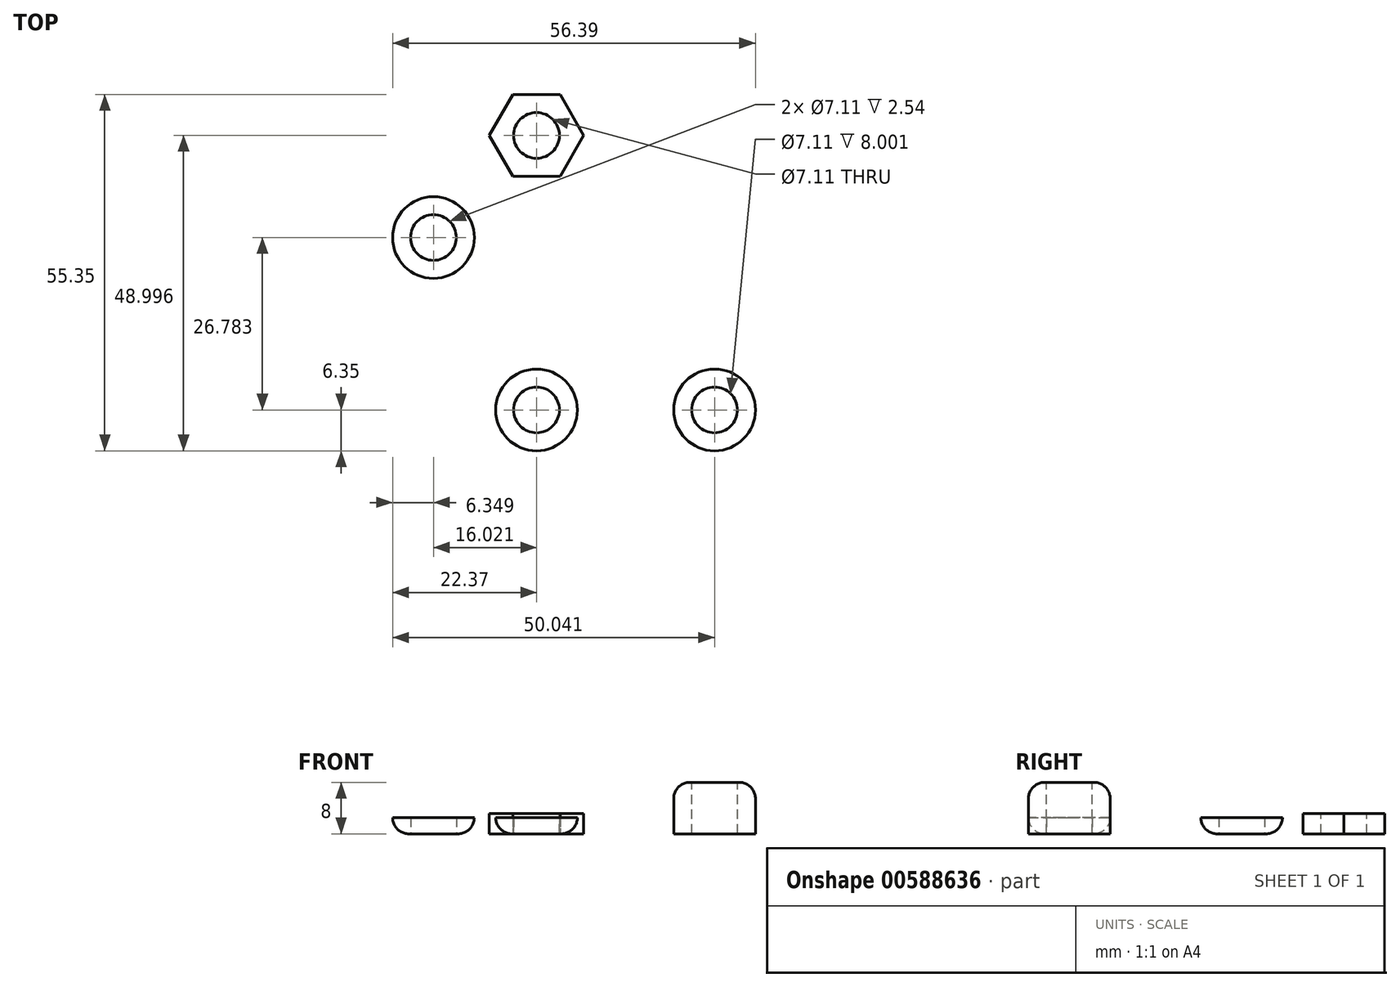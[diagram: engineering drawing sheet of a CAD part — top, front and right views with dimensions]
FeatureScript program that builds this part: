
annotation { "Feature Type Name" : "Feature", "Feature Type Description" : "" }
export const myFeature = defineFeature(function(context is Context, id is Id, definition is map)
    precondition{}
    {
        {
            var Q0;
            Q0=qCreatedBy(makeId("Top.planeOp"),FACE);
            var sketch = newSketch(context, id + "F0", { "sketchPlane" : qUnion([Q0])});
            skCircle(sketch, "E0", {"center": v(0, 0) * mm, "radius": 6.35 * mm});
            skCircle(sketch, "E1", {"center": v(-16.02, 26.78) * mm, "radius": 6.35 * mm});
            skSolve(sketch);
        }
        {
            var Q0;
            Q0 = qSketchRegion(id + "F0", true);
            extrude(context, id + "F1", {"entities" : qUnion([Q0]), "depth" : 2.54 * mm, "offsetDistance" : 25.4 * mm});
        }
        {
            var Q0;
            Q0=makeQuery(id+"F1.opExtrude","CAP_EDGE",EDGE,{"disambiguationData":[OSD([sQuery(id+"F0.wireOp",EDGE,"E0")])],"isStart":true});
            var Q1;
            Q1=makeQuery(id+"F1.opExtrude","CAP_EDGE",EDGE,{"disambiguationData":[OSD([sQuery(id+"F0.wireOp",EDGE,"E1")])],"isStart":true});
            fillet(context, id + "F2", {"entities" : qUnion([Q0, Q1]), "radius" : 2.54 * mm, "tangentPropagation" : true, "allowEdgeOverflow" : false});
        }
        {
            var Q0;
            Q0=makeQuery(id+"F1.opExtrude","CAP_FACE",FACE,{"disambiguationData":[OSD([sQuery(id+"F0.wireOp",EDGE,"E0")])],"isStart":true});
            var sketch = newSketch(context, id + "F3", { "sketchPlane" : qUnion([Q0])});
            skCircle(sketch, "E2", {"center": v(0, 0) * mm, "radius": 3.56 * mm});
            skSolve(sketch);
        }
        {
            var Q0;
            Q0 = qSketchRegion(id + "F3", true);
            extrude(context, id + "F4", {"entities" : qUnion([Q0]), "operationType" : NewBodyOperationType.REMOVE, "oppositeDirection" : true, "depth" : 2.54 * mm, "offsetDistance" : 25.4 * mm});
        }
        {
            var Q0;
            Q0=makeQuery(id+"F1.opExtrude","CAP_FACE",FACE,{"disambiguationData":[OSD([sQuery(id+"F0.wireOp",EDGE,"E1")])],"isStart":true});
            var sketch = newSketch(context, id + "F5", { "sketchPlane" : qUnion([Q0])});
            skCircle(sketch, "E3", {"center": v(-16.02, -26.78) * mm, "radius": 3.56 * mm});
            skSolve(sketch);
        }
        {
            var Q0;
            Q0 = qSketchRegion(id + "F5", true);
            extrude(context, id + "F6", {"entities" : qUnion([Q0]), "operationType" : NewBodyOperationType.REMOVE, "oppositeDirection" : true, "depth" : 2.54 * mm, "offsetDistance" : 25.4 * mm});
        }
        {
            var Q0;
            Q0=qCreatedBy(makeId("Top.planeOp"),FACE);
            var sketch = newSketch(context, id + "F7", { "sketchPlane" : qUnion([Q0])});
            skCircle(sketch, "E4", {"center": v(27.67, 0) * mm, "radius": 6.35 * mm});
            skSolve(sketch);
        }
        {
            var Q0;
            Q0=makeQuery(id+"F7.imprint","IMPRINT",FACE,{"disambiguationData":[TD([[makeQuery(id+"F7.imprint","IMPRINT",EDGE,{"derivedFrom":sQuery(id+"F7.wireOp",EDGE,"E4")}),1.0]])]});
            extrude(context, id + "F8", {"entities" : qUnion([Q0]), "depth" : 8 * mm, "offsetDistance" : 25.4 * mm});
        }
        {
            var Q0;
            Q0=makeQuery(id+"F8.opExtrude","CAP_EDGE",EDGE,{"disambiguationData":[OSD([sQuery(id+"F7.wireOp",EDGE,"TgdO63bO-GpAG-Yatk-n7lf-2ucI2Jy1ILUc")])],"isStart":false});
            var Q1;
            Q1=makeQuery(id+"F8.opExtrude","CAP_EDGE",EDGE,{"disambiguationData":[OSD([sQuery(id+"F7.wireOp",EDGE,"E4")])],"isStart":false});
            fillet(context, id + "F9", {"entities" : qUnion([Q0, Q1]), "radius" : 2.54 * mm, "tangentPropagation" : true, "allowEdgeOverflow" : false});
        }
        {
            var Q0;
            Q0=makeQuery(id+"F8.opExtrude","CAP_FACE",FACE,{"disambiguationData":[OSD([sQuery(id+"F7.wireOp",EDGE,"E4")])],"isStart":false});
            var sketch = newSketch(context, id + "F10", { "sketchPlane" : qUnion([Q0])});
            skSolve(sketch);
        }
        {
            var Q0;
            {var subQ0=sQuery(id+"F7.wireOp",EDGE,"E4");Q0=makeQuery(id+"F10.imprint","IMPRINT",FACE,{"disambiguationData":[TD([[makeQuery(id+"F10.imprint","IMPRINT",EDGE,{"derivedFrom":makeQuery(id+"F9.opFillet","BLEND_EDGE",EDGE,{"blendedFrom":[makeQuery(id+"F8.opExtrude","CAP_EDGE",EDGE,{"disambiguationData":[OSD([subQ0])],"isStart":false}),makeQuery(id+"F8.opExtrude","CAP_FACE",FACE,{"disambiguationData":[OSD([subQ0])],"isStart":false})],"blendedInto":[makeQuery(id+"F8.opExtrude","CAP_FACE",FACE,{"disambiguationData":[OSD([subQ0])],"isStart":false})]})}),1.0]])]});}
            var sketch = newSketch(context, id + "F11", { "sketchPlane" : qUnion([Q0])});
            skCircle(sketch, "E5", {"center": v(27.67, 0) * mm, "radius": 3.56 * mm});
            skSolve(sketch);
        }
        {
            var Q0;
            Q0 = qSketchRegion(id + "F11", true);
            extrude(context, id + "F12", {"entities" : qUnion([Q0]), "operationType" : NewBodyOperationType.REMOVE, "oppositeDirection" : true, "depth" : 11.15 * mm, "offsetDistance" : 25.4 * mm});
        }
        {
            var Q0;
            Q0=qCreatedBy(makeId("Top.planeOp"),FACE);
            var sketch = newSketch(context, id + "F13", { "sketchPlane" : qUnion([Q0])});
            skLineSegment(sketch, "E6.0", {"start": v(3.67, 36.3) * mm, "end": v(-3.67, 36.3) * mm});
            skLineSegment(sketch, "E6.1", {"start": v(-3.67, 36.3) * mm, "end": v(-7.33, 42.65) * mm});
            skLineSegment(sketch, "E6.2", {"start": v(-7.33, 42.65) * mm, "end": v(-3.67, 49) * mm});
            skLineSegment(sketch, "E6.3", {"start": v(-3.67, 49) * mm, "end": v(3.67, 49) * mm});
            skLineSegment(sketch, "E6.4", {"start": v(3.67, 49) * mm, "end": v(7.33, 42.65) * mm});
            skLineSegment(sketch, "E6.5", {"start": v(7.33, 42.65) * mm, "end": v(3.67, 36.3) * mm});
            skPoint(sketch, "E6.0.midPoint", {"position": v(0, 36.3) * mm});
            skSolve(sketch);
        }
        {
            var Q0;
            Q0=makeQuery(id+"F13.imprint","IMPRINT",FACE,{"disambiguationData":[TD([[makeQuery(id+"F13.imprint","IMPRINT",EDGE,{"derivedFrom":sQuery(id+"F13.wireOp",EDGE,"E6.0")}),-1.0]])]});
            extrude(context, id + "F14", {"entities" : qUnion([Q0]), "depth" : 3.17 * mm, "offsetDistance" : 25.4 * mm});
        }
        {
            var Q0;
            Q0=makeQuery(id+"F14.opExtrude","CAP_FACE",FACE,{"disambiguationData":[OSD([sQuery(id+"F13.wireOp",EDGE,"E6.0"),sQuery(id+"F13.wireOp",EDGE,"E6.1"),sQuery(id+"F13.wireOp",EDGE,"E6.2"),sQuery(id+"F13.wireOp",EDGE,"E6.3"),sQuery(id+"F13.wireOp",EDGE,"E6.4"),sQuery(id+"F13.wireOp",EDGE,"E6.5")])],"isStart":false});
            var sketch = newSketch(context, id + "F15", { "sketchPlane" : qUnion([Q0])});
            skCircle(sketch, "E7", {"center": v(0, 42.65) * mm, "radius": 3.56 * mm});
            skSolve(sketch);
        }
        {
            var Q0;
            Q0 = qSketchRegion(id + "F15", true);
            extrude(context, id + "F16", {"entities" : qUnion([Q0]), "operationType" : NewBodyOperationType.REMOVE, "oppositeDirection" : true, "depth" : 3.17 * mm, "offsetDistance" : 25.4 * mm});
        }
    });
